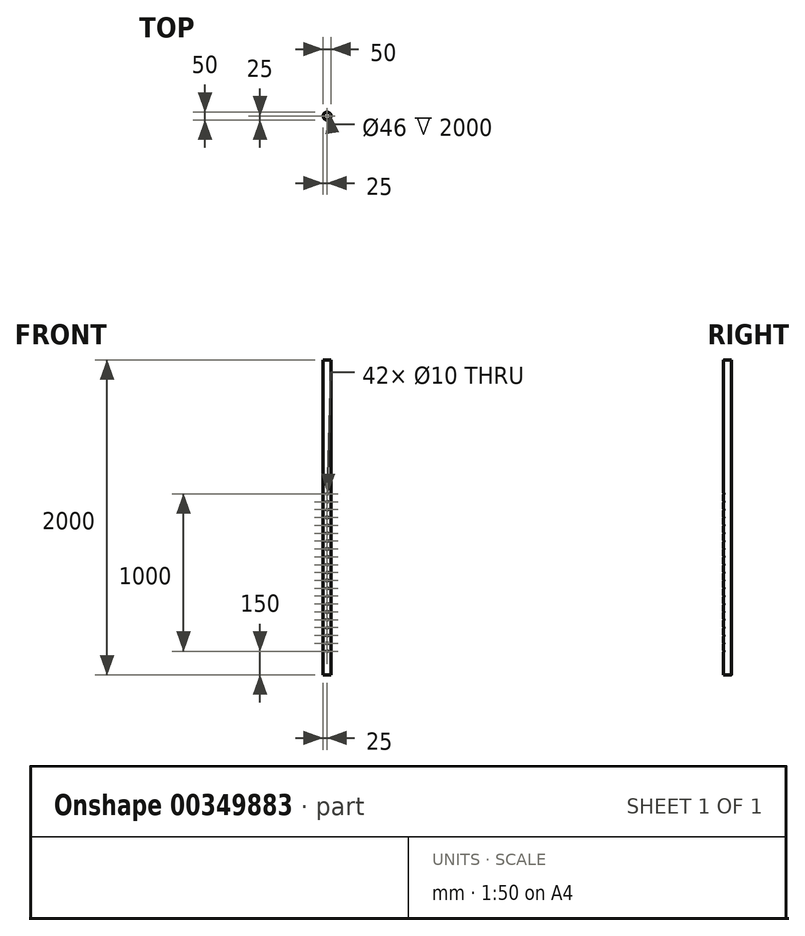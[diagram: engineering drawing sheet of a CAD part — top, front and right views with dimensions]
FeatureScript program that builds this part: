
annotation { "Feature Type Name" : "Feature", "Feature Type Description" : "" }
export const myFeature = defineFeature(function(context is Context, id is Id, definition is map)
    precondition{}
    {
        {
            var Q0;
            Q0=qCreatedBy(makeId("Top.planeOp"),FACE);
            var sketch = newSketch(context, id + "F0", { "sketchPlane" : qUnion([Q0])});
            skCircle(sketch, "E0", {"center": v(0, 0) * mm, "radius": 25 * mm});
            skCircle(sketch, "E1", {"center": v(0, 0) * mm, "radius": 23 * mm});
            skSolve(sketch);
        }
        {
            var Q0;
            Q0=makeQuery(id+"F0.imprint","IMPRINT",FACE,{"disambiguationData":[TD([[makeQuery(id+"F0.imprint","IMPRINT",EDGE,{"derivedFrom":sQuery(id+"F0.wireOp",EDGE,"E0")}),1.0]])]});
            extrude(context, id + "F1", {"entities" : qUnion([Q0]), "depth" : 2000 * mm});
        }
        {
            var Q0;
            Q0=qCreatedBy(makeId("Front.planeOp"),FACE);
            cPlane(context, id + "F2", {"entities" : qUnion([Q0]), "cplaneType" : CPlaneType.OFFSET, "offset" : 50 * mm, "width" : 150 * mm, "height" : 150 * mm});
        }
        {
            var Q0;
            Q0=qCreatedBy(id+"F2.planeOp",FACE);
            var sketch = newSketch(context, id + "F3", { "sketchPlane" : qUnion([Q0])});
            skCircle(sketch, "E2", {"center": v(0, 150) * mm, "radius": 5 * mm});
            skCircle(sketch, "E3.0.1.0", {"center": v(0, 200) * mm, "radius": 5 * mm});
            skCircle(sketch, "E3.0.2.0", {"center": v(0, 250) * mm, "radius": 5 * mm});
            skCircle(sketch, "E3.0.3.0", {"center": v(0, 300) * mm, "radius": 5 * mm});
            skCircle(sketch, "E3.0.4.0", {"center": v(0, 350) * mm, "radius": 5 * mm});
            skCircle(sketch, "E3.0.5.0", {"center": v(0, 400) * mm, "radius": 5 * mm});
            skCircle(sketch, "E3.0.6.0", {"center": v(0, 450) * mm, "radius": 5 * mm});
            skCircle(sketch, "E3.0.7.0", {"center": v(0, 500) * mm, "radius": 5 * mm});
            skCircle(sketch, "E3.0.8.0", {"center": v(0, 550) * mm, "radius": 5 * mm});
            skCircle(sketch, "E3.0.9.0", {"center": v(0, 600) * mm, "radius": 5 * mm});
            skCircle(sketch, "E3.0.10.0", {"center": v(0, 650) * mm, "radius": 5 * mm});
            skCircle(sketch, "E3.0.11.0", {"center": v(0, 700) * mm, "radius": 5 * mm});
            skCircle(sketch, "E3.0.12.0", {"center": v(0, 750) * mm, "radius": 5 * mm});
            skCircle(sketch, "E3.0.13.0", {"center": v(0, 800) * mm, "radius": 5 * mm});
            skCircle(sketch, "E3.0.14.0", {"center": v(0, 850) * mm, "radius": 5 * mm});
            skCircle(sketch, "E3.0.15.0", {"center": v(0, 900) * mm, "radius": 5 * mm});
            skCircle(sketch, "E3.0.16.0", {"center": v(0, 950) * mm, "radius": 5 * mm});
            skCircle(sketch, "E3.0.17.0", {"center": v(0, 1000) * mm, "radius": 5 * mm});
            skLineSegment(sketch, "E3.direction1", {"start": v(0, 150) * mm, "end": v(25, 150) * mm, "construction": true});
            skLineSegment(sketch, "E3.direction2", {"start": v(0, 150) * mm, "end": v(0, 200) * mm, "construction": true});
            skCircle(sketch, "E4.0.0.18", {"center": v(0, 1050) * mm, "radius": 5 * mm});
            skCircle(sketch, "E4.0.0.19", {"center": v(0, 1100) * mm, "radius": 5 * mm});
            skCircle(sketch, "E4.0.0.20", {"center": v(0, 1150) * mm, "radius": 5 * mm});
            skSolve(sketch);
        }
        {
            var Q0;
            Q0 = qSketchRegion(id + "F3", true);
            extrude(context, id + "F4", {"entities" : qUnion([Q0]), "operationType" : NewBodyOperationType.REMOVE, "oppositeDirection" : true, "depth" : 90 * mm});
        }
    });
